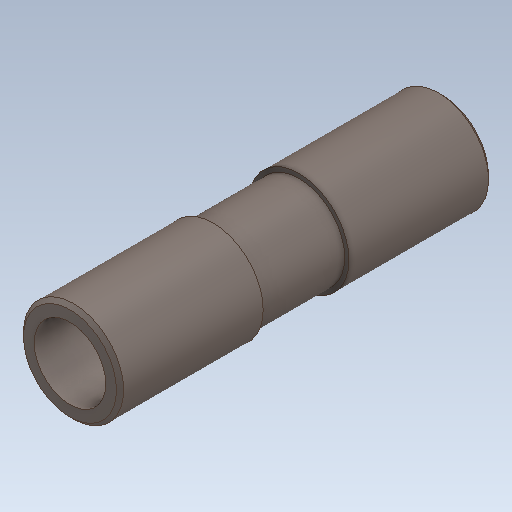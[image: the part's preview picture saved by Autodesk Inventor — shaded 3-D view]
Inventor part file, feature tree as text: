
AUTODESK INVENTOR PART (.ipt)
format: ipt  version: 2020 (Build 240168000, 168)  size: 122,368 bytes
history: native  units: in
note: dims shown in document units (in); Inventor stores cm internally (conversion verified against a paired STEP export)
features: chamfer x1
ambient origin geometry x8: Origin, YZ Plane, XZ Plane, XY Plane, X Axis, Y Axis, Z Axis, Center Point
bodies: Solid1 (feature_tree)
feature tree (1):
  chamfer  "Chamfer1"  [1 undecoded]
note: 1 required parameter value undecoded (feature->parameter linkage not recoverable at this tier; creation-order binding heuristic only, values carry confidence <= 0.55)
